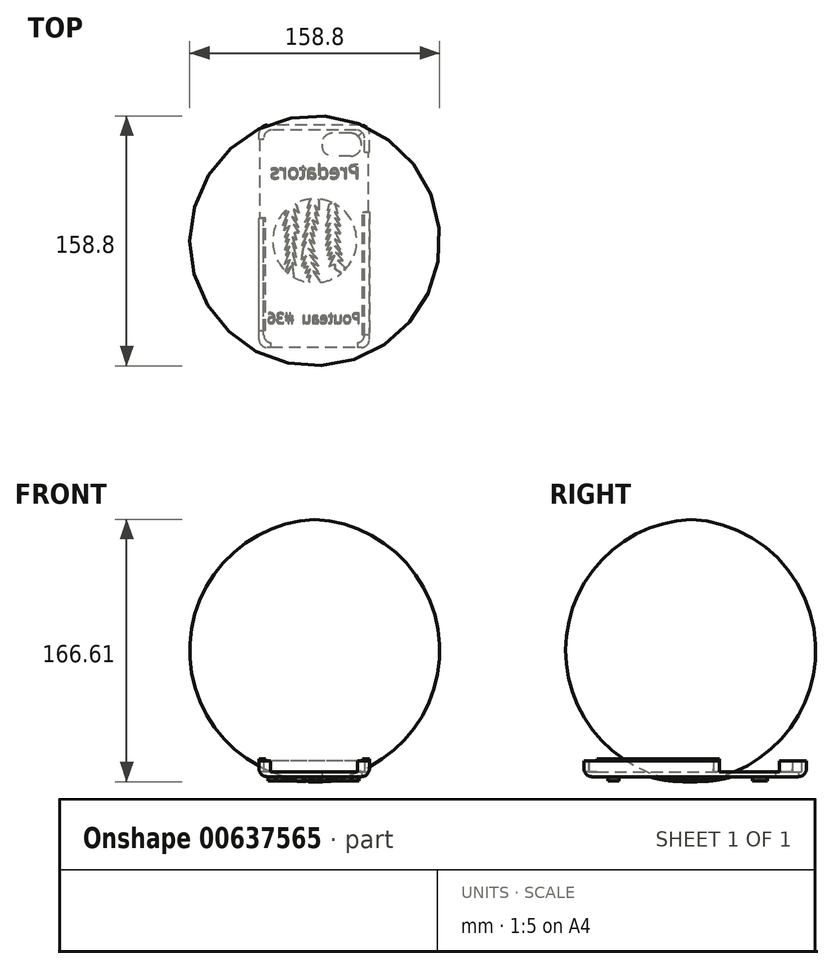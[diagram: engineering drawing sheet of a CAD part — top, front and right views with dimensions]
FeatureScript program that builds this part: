
annotation { "Feature Type Name" : "Feature", "Feature Type Description" : "" }
export const myFeature = defineFeature(function(context is Context, id is Id, definition is map)
    precondition{}
    {
        {
            var Q0;
            Q0=qCreatedBy(makeId("Top.planeOp"),FACE);
            var sketch = newSketch(context, id + "F0", { "sketchPlane" : qUnion([Q0])});
            skLineSegment(sketch, "E0.bottom", {"start": v(34.68, -26.2) * mm, "end": v(-35.42, -26.2) * mm});
            skLineSegment(sketch, "E0.top", {"start": v(34.68, 115.03) * mm, "end": v(-35.42, 115.03) * mm});
            skLineSegment(sketch, "E0.left", {"start": v(34.68, -26.2) * mm, "end": v(34.68, 115.03) * mm});
            skLineSegment(sketch, "E0.right", {"start": v(-35.42, -26.2) * mm, "end": v(-35.42, 115.03) * mm});
            skSolve(sketch);
        }
        {
            var Q0;
            Q0=makeQuery(id+"F0.imprint","IMPRINT",FACE,{"disambiguationData":[TD([[makeQuery(id+"F0.imprint","IMPRINT",EDGE,{"derivedFrom":sQuery(id+"F0.wireOp",EDGE,"E0.bottom")}),-1.0]])]});
            extrude(context, id + "F1", {"entities" : qUnion([Q0]), "depth" : 9.9 * mm, "offsetDistance" : 25.4 * mm});
        }
        {
            var Q0;
            Q0=makeQuery(id+"F1.opExtrude","CAP_FACE",FACE,{"disambiguationData":[OSD([sQuery(id+"F0.wireOp",EDGE,"E0.bottom"),sQuery(id+"F0.wireOp",EDGE,"E0.top"),sQuery(id+"F0.wireOp",EDGE,"E0.left"),sQuery(id+"F0.wireOp",EDGE,"E0.right")])],"isStart":false});
            shell(context, id + "F2", {"entities" : qUnion([Q0]), "thickness" : 3.05 * mm});
        }
        {
            var Q0;
            Q0=makeQuery(id+"F1.opExtrude","SWEPT_EDGE",EDGE,{"disambiguationData":[OSD([sQuery(id+"F0.wireOp",EDGE,"E0.top"),sQuery(id+"F0.wireOp",EDGE,"E0.right")])]});
            fillet(context, id + "F3", {"entities" : qUnion([Q0]), "radius" : 5.08 * mm, "tangentPropagation" : true, "allowEdgeOverflow" : false});
        }
        {
            var Q0;
            Q0=makeQuery(id+"F1.opExtrude","SWEPT_FACE",FACE,{"disambiguationData":[OSD([sQuery(id+"F0.wireOp",EDGE,"E0.right")])]});
            var sketch = newSketch(context, id + "F4", { "sketchPlane" : qUnion([Q0])});
            skLineSegment(sketch, "E1.bottom", {"start": v(-106.04, 9.9) * mm, "end": v(-56.04, 9.9) * mm});
            skLineSegment(sketch, "E1.top", {"start": v(-106.04, 3.05) * mm, "end": v(-56.04, 3.05) * mm});
            skLineSegment(sketch, "E1.left", {"start": v(-106.04, 9.9) * mm, "end": v(-106.04, 3.05) * mm});
            skLineSegment(sketch, "E1.right", {"start": v(-56.04, 9.9) * mm, "end": v(-56.04, 3.05) * mm});
            skSolve(sketch);
        }
        {
            var Q0;
            Q0=makeQuery(id+"F4.imprint","IMPRINT",FACE,{"disambiguationData":[TD([[makeQuery(id+"F4.imprint","IMPRINT",EDGE,{"derivedFrom":sQuery(id+"F4.wireOp",EDGE,"E1.bottom")}),1.0]])]});
            extrude(context, id + "F5", {"entities" : qUnion([Q0]), "operationType" : NewBodyOperationType.REMOVE, "oppositeDirection" : true, "depth" : 3.05 * mm, "offsetDistance" : 25.4 * mm});
        }
        {
            var Q0;
            Q0=makeQuery(id+"F1.opExtrude","SWEPT_FACE",FACE,{"disambiguationData":[OSD([sQuery(id+"F0.wireOp",EDGE,"E0.left")])]});
            var sketch = newSketch(context, id + "F6", { "sketchPlane" : qUnion([Q0])});
            skLineSegment(sketch, "E2.bottom", {"start": v(98, 9.9) * mm, "end": v(59.9, 9.9) * mm});
            skLineSegment(sketch, "E2.top", {"start": v(98, 3.05) * mm, "end": v(59.9, 3.05) * mm});
            skLineSegment(sketch, "E2.left", {"start": v(98, 9.9) * mm, "end": v(98, 3.05) * mm});
            skLineSegment(sketch, "E2.right", {"start": v(59.9, 9.9) * mm, "end": v(59.9, 3.05) * mm});
            skSolve(sketch);
        }
        {
            var Q0;
            Q0=makeQuery(id+"F6.imprint","IMPRINT",FACE,{"disambiguationData":[TD([[makeQuery(id+"F6.imprint","IMPRINT",EDGE,{"derivedFrom":sQuery(id+"F6.wireOp",EDGE,"E2.bottom")}),-1.0]])]});
            extrude(context, id + "F7", {"entities" : qUnion([Q0]), "operationType" : NewBodyOperationType.REMOVE, "oppositeDirection" : true, "depth" : 3.05 * mm, "offsetDistance" : 25.4 * mm});
        }
        {
            var Q0;
            Q0=makeQuery(id+"F1.opExtrude","SWEPT_EDGE",EDGE,{"disambiguationData":[OSD([sQuery(id+"F0.wireOp",EDGE,"E0.top"),sQuery(id+"F0.wireOp",EDGE,"E0.left")])]});
            var Q1;
            Q1=makeQuery(id+"F2.opShell","OFFSET_EDGE",EDGE,{"disambiguationData":[OSD([sQuery(id+"F0.wireOp",EDGE,"E0.top"),sQuery(id+"F0.wireOp",EDGE,"E0.left")])]});
            var Q2;
            Q2=makeQuery(id+"F2.opShell","OFFSET_EDGE",EDGE,{"disambiguationData":[OSD([sQuery(id+"F0.wireOp",EDGE,"E0.top"),sQuery(id+"F0.wireOp",EDGE,"E0.right")])]});
            var Q3;
            Q3=makeQuery(id+"F1.opExtrude","SWEPT_EDGE",EDGE,{"disambiguationData":[OSD([sQuery(id+"F0.wireOp",EDGE,"E0.bottom"),sQuery(id+"F0.wireOp",EDGE,"E0.left")])]});
            var Q4;
            Q4=makeQuery(id+"F1.opExtrude","SWEPT_EDGE",EDGE,{"disambiguationData":[OSD([sQuery(id+"F0.wireOp",EDGE,"E0.bottom"),sQuery(id+"F0.wireOp",EDGE,"E0.right")])]});
            var Q5;
            Q5=makeQuery(id+"F2.opShell","OFFSET_EDGE",EDGE,{"disambiguationData":[OSD([sQuery(id+"F0.wireOp",EDGE,"E0.bottom"),sQuery(id+"F0.wireOp",EDGE,"E0.right")])]});
            var Q6;
            Q6=makeQuery(id+"F2.opShell","OFFSET_EDGE",EDGE,{"disambiguationData":[OSD([sQuery(id+"F0.wireOp",EDGE,"E0.bottom"),sQuery(id+"F0.wireOp",EDGE,"E0.left")])]});
            fillet(context, id + "F8", {"entities" : qUnion([Q0, Q1, Q2, Q3, Q4, Q5, Q6]), "radius" : 5.08 * mm, "tangentPropagation" : true, "allowEdgeOverflow" : false});
        }
        {
            var Q0;
            Q0=makeQuery(id+"F1.opExtrude","SWEPT_FACE",FACE,{"disambiguationData":[OSD([sQuery(id+"F0.wireOp",EDGE,"E0.bottom")])]});
            var sketch = newSketch(context, id + "F9", { "sketchPlane" : qUnion([Q0])});
            skLineSegment(sketch, "E3.bottom", {"start": v(-27.96, 9.9) * mm, "end": v(27.04, 9.9) * mm});
            skLineSegment(sketch, "E3.top", {"start": v(-27.96, 3.05) * mm, "end": v(27.04, 3.05) * mm});
            skLineSegment(sketch, "E3.left", {"start": v(-27.96, 9.9) * mm, "end": v(-27.96, 3.05) * mm});
            skLineSegment(sketch, "E3.right", {"start": v(27.04, 9.9) * mm, "end": v(27.04, 3.05) * mm});
            skSolve(sketch);
        }
        {
            var Q0;
            Q0=makeQuery(id+"F9.imprint","IMPRINT",FACE,{"disambiguationData":[TD([[makeQuery(id+"F9.imprint","IMPRINT",EDGE,{"derivedFrom":sQuery(id+"F9.wireOp",EDGE,"E3.bottom")}),1.0]])]});
            extrude(context, id + "F10", {"entities" : qUnion([Q0]), "operationType" : NewBodyOperationType.REMOVE, "oppositeDirection" : true, "depth" : 3.56 * mm, "offsetDistance" : 25.4 * mm});
        }
        {
            var Q0;
            Q0=makeQuery(id+"F1.opExtrude","CAP_EDGE",EDGE,{"disambiguationData":[OSD([sQuery(id+"F0.wireOp",EDGE,"E0.top")])],"isStart":true});
            var Q1;
            Q1=makeQuery(id+"F1.opExtrude","CAP_FACE",FACE,{"disambiguationData":[OSD([sQuery(id+"F0.wireOp",EDGE,"E0.bottom"),sQuery(id+"F0.wireOp",EDGE,"E0.top"),sQuery(id+"F0.wireOp",EDGE,"E0.left"),sQuery(id+"F0.wireOp",EDGE,"E0.right")])],"isStart":true});
            fillet(context, id + "F11", {"entities" : qUnion([Q0, Q1]), "radius" : 5.08 * mm, "tangentPropagation" : true, "allowEdgeOverflow" : false});
        }
        {
            var Q0;
            Q0=makeQuery(id+"F1.opExtrude","CAP_FACE",FACE,{"disambiguationData":[OSD([sQuery(id+"F0.wireOp",EDGE,"E0.bottom"),sQuery(id+"F0.wireOp",EDGE,"E0.top"),sQuery(id+"F0.wireOp",EDGE,"E0.left"),sQuery(id+"F0.wireOp",EDGE,"E0.right")])],"isStart":true});
            var sketch = newSketch(context, id + "F12", { "sketchPlane" : qUnion([Q0])});
            skLineSegment(sketch, "E4.bottom", {"start": v(29.6, -109.95) * mm, "end": v(4.52, -109.95) * mm});
            skLineSegment(sketch, "E4.top", {"start": v(29.6, -95.42) * mm, "end": v(4.52, -95.42) * mm});
            skLineSegment(sketch, "E4.left", {"start": v(29.6, -109.95) * mm, "end": v(29.6, -95.42) * mm});
            skLineSegment(sketch, "E4.right", {"start": v(4.52, -109.95) * mm, "end": v(4.52, -95.42) * mm});
            skSolve(sketch);
        }
        {
            var Q0;
            Q0=makeQuery(id+"F12.imprint","IMPRINT",FACE,{"disambiguationData":[TD([[makeQuery(id+"F12.imprint","IMPRINT",EDGE,{"derivedFrom":sQuery(id+"F12.wireOp",EDGE,"E4.bottom")}),1.0]])]});
            extrude(context, id + "F13", {"entities" : qUnion([Q0]), "operationType" : NewBodyOperationType.REMOVE, "oppositeDirection" : true, "depth" : 3.05 * mm, "offsetDistance" : 25.4 * mm});
        }
        {
            var Q0;
            {var subQ0=sQuery(id+"F0.wireOp",EDGE,"E0.bottom");var subQ2=sQuery(id+"F0.wireOp",EDGE,"E0.left");Q0=makeQuery(id+"F7.boolean.opBoolean","SPLIT",FACE,{"disambiguationData":[TD([makeQuery(id+"F2.opShell","OFFSET_FACE",FACE,{"disambiguationData":[OSD([subQ0])]})])],"derivedFrom":makeQuery(id+"F2.opShell","OFFSET_FACE",FACE,{"disambiguationData":[OSD([subQ2])]})});}
            var sketch = newSketch(context, id + "F14", { "sketchPlane" : qUnion([Q0])});
            skLineSegment(sketch, "E5.bottom", {"start": v(-59.9, 9.9) * mm, "end": v(18.07, 9.9) * mm});
            skLineSegment(sketch, "E5.top", {"start": v(-59.9, 11.18) * mm, "end": v(18.07, 11.18) * mm});
            skLineSegment(sketch, "E5.left", {"start": v(-59.9, 9.9) * mm, "end": v(-59.9, 11.18) * mm});
            skLineSegment(sketch, "E5.right", {"start": v(18.07, 9.9) * mm, "end": v(18.07, 11.18) * mm});
            skSolve(sketch);
        }
        {
            var Q0;
            Q0 = qSketchRegion(id + "F14", true);
            extrude(context, id + "F15", {"entities" : qUnion([Q0]), "depth" : 1.27 * mm, "offsetDistance" : 25.4 * mm});
        }
        {
            var Q0;
            Q0=makeQuery(id+"F15.opExtrude","CAP_FACE",FACE,{"disambiguationData":[OSD([sQuery(id+"F14.wireOp",EDGE,"E5.bottom"),sQuery(id+"F14.wireOp",EDGE,"E5.top"),sQuery(id+"F14.wireOp",EDGE,"E5.left"),sQuery(id+"F14.wireOp",EDGE,"E5.right")])],"isStart":true});
            extrude(context, id + "F16", {"entities" : qUnion([Q0]), "depth" : 3.05 * mm, "offsetDistance" : 25.4 * mm});
        }
        {
            var Q0;
            {var subQ0=sQuery(id+"F0.wireOp",EDGE,"E0.bottom");var subQ1=sQuery(id+"F0.wireOp",EDGE,"E0.right");Q0=makeQuery(id+"F5.boolean.opBoolean","SPLIT",FACE,{"disambiguationData":[TD([makeQuery(id+"F2.opShell","OFFSET_FACE",FACE,{"disambiguationData":[OSD([subQ0])]})])],"derivedFrom":makeQuery(id+"F2.opShell","OFFSET_FACE",FACE,{"disambiguationData":[OSD([subQ1])]})});}
            var sketch = newSketch(context, id + "F17", { "sketchPlane" : qUnion([Q0])});
            skLineSegment(sketch, "E6.bottom", {"start": v(56.04, 9.9) * mm, "end": v(-15.42, 9.9) * mm});
            skLineSegment(sketch, "E6.top", {"start": v(56.04, 11.18) * mm, "end": v(-15.42, 11.18) * mm});
            skLineSegment(sketch, "E6.left", {"start": v(56.04, 9.9) * mm, "end": v(56.04, 11.18) * mm});
            skLineSegment(sketch, "E6.right", {"start": v(-15.42, 9.9) * mm, "end": v(-15.42, 11.18) * mm});
            skSolve(sketch);
        }
        {
            var Q0;
            Q0=makeQuery(id+"F17.imprint","IMPRINT",FACE,{"disambiguationData":[TD([[makeQuery(id+"F17.imprint","IMPRINT",EDGE,{"derivedFrom":sQuery(id+"F17.wireOp",EDGE,"E6.bottom")}),1.0]])]});
            extrude(context, id + "F18", {"entities" : qUnion([Q0]), "depth" : 1.27 * mm, "offsetDistance" : 25.4 * mm});
        }
        {
            var Q0;
            Q0=makeQuery(id+"F18.opExtrude","CAP_FACE",FACE,{"disambiguationData":[OSD([sQuery(id+"F17.wireOp",EDGE,"E6.bottom"),sQuery(id+"F17.wireOp",EDGE,"E6.top"),sQuery(id+"F17.wireOp",EDGE,"E6.left"),sQuery(id+"F17.wireOp",EDGE,"E6.right")])],"isStart":true});
            extrude(context, id + "F19", {"entities" : qUnion([Q0]), "depth" : 3.05 * mm, "offsetDistance" : 25.4 * mm});
        }
        {
            var Q0;
            Q0=makeQuery(id+"F1.opExtrude","CAP_FACE",FACE,{"disambiguationData":[OSD([sQuery(id+"F0.wireOp",EDGE,"E0.bottom"),sQuery(id+"F0.wireOp",EDGE,"E0.top"),sQuery(id+"F0.wireOp",EDGE,"E0.left"),sQuery(id+"F0.wireOp",EDGE,"E0.right")])],"isStart":true});
            var sketch = newSketch(context, id + "F20", { "sketchPlane" : qUnion([Q0])});
            skText(sketch, "E7", { "text": "Predators\n", "fontName": "OpenSans-Regular.ttf"});
            skPoint(sketch, "E8.center.orphan", {"position": v(0, -41.54) * mm});
            const initialGuessF20  = {"E7": [0.02862, -0.08103, -1, 0, 0.00896]};
            skSetInitialGuess(sketch, initialGuessF20);
            skSolve(sketch);
        }
        {
            var Q0;
            Q0=qCreatedBy(makeId("Right.planeOp"),FACE);
            var sketch = newSketch(context, id + "F21", { "sketchPlane" : qUnion([Q0])});
            skLineSegment(sketch, "E9", {"start": v(41.6, 0) * mm, "end": v(41.6, -3.06) * mm});
            skArc(sketch, "E10", {"start": v(14.92, 0) * mm, "mid": v(28.13, -2.61) * mm, "end": v(41.6, -3.06) * mm});
            skLineSegment(sketch, "E11", {"start": v(41.6, 0) * mm, "end": v(14.92, 0) * mm});
            skSolve(sketch);
        }
        {
            var Q0;
            Q0=makeQuery(id+"F21.imprint","IMPRINT",FACE,{"disambiguationData":[TD([[makeQuery(id+"F21.imprint","IMPRINT",EDGE,{"derivedFrom":sQuery(id+"F21.wireOp",EDGE,"E9")}),-1.0]])]});
            var Q1;
            Q1=sQuery(id+"F21.wireOp",EDGE,"E9");
            revolve(context, id + "F22", {"operationType" : NewBodyOperationType.ADD, "entities" : qUnion([Q0]), "axis" : qUnion([Q1]), "revolveType" : RevolveType.FULL});
        }
        {
            var Q0;
            Q0=makeQuery(id+"F20.imprint","IMPRINT",FACE,{"disambiguationData":[TD([[makeQuery(id+"F20.imprint","IMPRINT",EDGE,{"derivedFrom":sQuery(id+"F20.wireOp",EDGE,"E7.sketch_text.stroke-0")}),1.0]])]});
            var sketch = newSketch(context, id + "F23", { "sketchPlane" : qUnion([Q0])});
            skLineSegment(sketch, "E12", {"start": v(13.28, -64.28) * mm, "end": v(14.6, -58.78) * mm});
            skLineSegment(sketch, "E13", {"start": v(14.6, -58.78) * mm, "end": v(12.69, -59.98) * mm});
            skLineSegment(sketch, "E14", {"start": v(12.69, -59.98) * mm, "end": v(15.8, -54.84) * mm});
            skLineSegment(sketch, "E15", {"start": v(15.8, -54.84) * mm, "end": v(12.8, -56.04) * mm});
            skLineSegment(sketch, "E16", {"start": v(12.8, -56.04) * mm, "end": v(16.27, -50.9) * mm});
            skLineSegment(sketch, "E17", {"start": v(16.27, -50.9) * mm, "end": v(12.69, -52.33) * mm});
            skLineSegment(sketch, "E18", {"start": v(12.69, -52.33) * mm, "end": v(16.27, -46.12) * mm});
            skLineSegment(sketch, "E19", {"start": v(16.27, -46.12) * mm, "end": v(13.04, -47.2) * mm});
            skLineSegment(sketch, "E20", {"start": v(13.04, -47.2) * mm, "end": v(16.27, -40.63) * mm});
            skLineSegment(sketch, "E21", {"start": v(16.27, -40.63) * mm, "end": v(12.69, -42.78) * mm});
            skLineSegment(sketch, "E22", {"start": v(12.69, -42.78) * mm, "end": v(16.27, -36.09) * mm});
            skLineSegment(sketch, "E23", {"start": v(16.27, -36.09) * mm, "end": v(12.8, -38.24) * mm});
            skLineSegment(sketch, "E24", {"start": v(12.8, -38.24) * mm, "end": v(17.34, -32.74) * mm});
            skLineSegment(sketch, "E25", {"start": v(17.34, -32.74) * mm, "end": v(13.28, -34.3) * mm});
            skLineSegment(sketch, "E26", {"start": v(13.28, -34.3) * mm, "end": v(18.06, -29.04) * mm});
            skLineSegment(sketch, "E27", {"start": v(18.06, -29.04) * mm, "end": v(14.6, -29.04) * mm});
            skLineSegment(sketch, "E28", {"start": v(14.6, -29.04) * mm, "end": v(18.9, -24.98) * mm});
            skLineSegment(sketch, "E29", {"start": v(9.22, -64.64) * mm, "end": v(8.15, -60.7) * mm});
            skLineSegment(sketch, "E30", {"start": v(8.15, -60.7) * mm, "end": v(9.46, -61.77) * mm});
            skLineSegment(sketch, "E31", {"start": v(9.46, -61.77) * mm, "end": v(7.87, -55.95) * mm});
            skLineSegment(sketch, "E32", {"start": v(7.87, -55.95) * mm, "end": v(9.82, -57.95) * mm});
            skLineSegment(sketch, "E33", {"start": v(9.82, -57.95) * mm, "end": v(6.95, -50.9) * mm});
            skLineSegment(sketch, "E34", {"start": v(6.95, -50.9) * mm, "end": v(9.94, -52.81) * mm});
            skLineSegment(sketch, "E35", {"start": v(9.94, -52.81) * mm, "end": v(6.95, -46.84) * mm});
            skLineSegment(sketch, "E36", {"start": v(6.95, -46.84) * mm, "end": v(9.94, -48.87) * mm});
            skLineSegment(sketch, "E37", {"start": v(9.94, -48.87) * mm, "end": v(6.95, -42.3) * mm});
            skLineSegment(sketch, "E38", {"start": v(6.95, -42.3) * mm, "end": v(10.18, -45.58) * mm});
            skPoint(sketch, "E38.endSnap0", {"position": v(8.44, -45.58) * mm});
            skLineSegment(sketch, "E39", {"start": v(10.18, -45.58) * mm, "end": v(6.95, -38.49) * mm});
            skLineSegment(sketch, "E40", {"start": v(6.95, -38.49) * mm, "end": v(10.06, -41.1) * mm});
            skLineSegment(sketch, "E41", {"start": v(10.06, -41.1) * mm, "end": v(7.64, -35.79) * mm});
            skLineSegment(sketch, "E42", {"start": v(7.64, -35.79) * mm, "end": v(10.3, -37.28) * mm});
            skLineSegment(sketch, "E43", {"start": v(10.3, -37.28) * mm, "end": v(8, -32.24) * mm});
            skLineSegment(sketch, "E44", {"start": v(8, -32.24) * mm, "end": v(11.01, -34.18) * mm});
            skLineSegment(sketch, "E45", {"start": v(11.01, -34.18) * mm, "end": v(8.94, -29.62) * mm});
            skLineSegment(sketch, "E46", {"start": v(8.94, -29.62) * mm, "end": v(12.45, -32.38) * mm});
            skLineSegment(sketch, "E47", {"start": v(12.45, -32.38) * mm, "end": v(9.2, -25.26) * mm});
            skLineSegment(sketch, "E48", {"start": v(9.2, -25.26) * mm, "end": v(12.92, -26.77) * mm});
            skLineSegment(sketch, "E49", {"start": v(12.92, -26.77) * mm, "end": v(12.92, -23.66) * mm});
            skLineSegment(sketch, "E50", {"start": v(13.28, -64.28) * mm, "end": v(11.5, -66.31) * mm});
            skLineSegment(sketch, "E51", {"start": v(11.5, -66.31) * mm, "end": v(9.22, -64.64) * mm});
            skLineSegment(sketch, "E52", {"start": v(18.9, -24.98) * mm, "end": v(18.9, -19.74) * mm});
            skLineSegment(sketch, "E53", {"start": v(18.9, -19.74) * mm, "end": v(12.92, -23.66) * mm});
            skLineSegment(sketch, "E54", {"start": v(2.8, -67.4) * mm, "end": v(2.8, -61.16) * mm});
            skLineSegment(sketch, "E55", {"start": v(2.8, -61.16) * mm, "end": v(0, -64.28) * mm});
            skLineSegment(sketch, "E56", {"start": v(0, -64.28) * mm, "end": v(2.5, -57.27) * mm});
            skLineSegment(sketch, "E57", {"start": v(2.5, -57.27) * mm, "end": v(0, -59.52) * mm});
            skLineSegment(sketch, "E58", {"start": v(0, -59.52) * mm, "end": v(2.04, -52.6) * mm});
            skLineSegment(sketch, "E59", {"start": v(2.04, -52.6) * mm, "end": v(-1.49, -54.89) * mm});
            skLineSegment(sketch, "E60", {"start": v(-1.49, -54.89) * mm, "end": v(1.22, -48.34) * mm});
            skLineSegment(sketch, "E61", {"start": v(1.22, -48.34) * mm, "end": v(-2, -50.8) * mm});
            skLineSegment(sketch, "E62", {"start": v(-2, -50.8) * mm, "end": v(0, -44.26) * mm});
            skLineSegment(sketch, "E63", {"start": v(0, -44.26) * mm, "end": v(-2.67, -46.74) * mm});
            skLineSegment(sketch, "E64", {"start": v(-2.67, -46.74) * mm, "end": v(0, -39.77) * mm});
            skLineSegment(sketch, "E65", {"start": v(0, -39.77) * mm, "end": v(-3.52, -42.28) * mm});
            skLineSegment(sketch, "E66", {"start": v(-3.52, -42.28) * mm, "end": v(0, -34.89) * mm});
            skLineSegment(sketch, "E67", {"start": v(0, -34.89) * mm, "end": v(-4.35, -36.85) * mm});
            skLineSegment(sketch, "E68", {"start": v(-4.35, -36.85) * mm, "end": v(1.75, -30.38) * mm});
            skLineSegment(sketch, "E69", {"start": v(1.75, -30.38) * mm, "end": v(-3.2, -32.52) * mm});
            skLineSegment(sketch, "E70", {"start": v(-3.2, -32.52) * mm, "end": v(2.57, -25.66) * mm});
            skLineSegment(sketch, "E71", {"start": v(2.57, -25.66) * mm, "end": v(-2.25, -27.8) * mm});
            skLineSegment(sketch, "E72", {"start": v(-2.25, -27.8) * mm, "end": v(2.9, -20.58) * mm});
            skLineSegment(sketch, "E73", {"start": v(2.9, -20.58) * mm, "end": v(-1.23, -22.5) * mm});
            skLineSegment(sketch, "E74", {"start": v(3.9, -15.08) * mm, "end": v(0, -11.67) * mm});
            skLineSegment(sketch, "E75", {"start": v(0, -11.67) * mm, "end": v(-3.8, -16.04) * mm});
            skLineSegment(sketch, "E76", {"start": v(2.8, -67.4) * mm, "end": v(0, -70.04) * mm});
            skLineSegment(sketch, "E77", {"start": v(0, -70.04) * mm, "end": v(-2.93, -67.4) * mm});
            skLineSegment(sketch, "E78", {"start": v(-2.93, -67.4) * mm, "end": v(-4.8, -62.23) * mm});
            skLineSegment(sketch, "E79", {"start": v(-4.8, -62.23) * mm, "end": v(-2.51, -64.28) * mm});
            skLineSegment(sketch, "E80", {"start": v(-2.51, -64.28) * mm, "end": v(-5.41, -57.38) * mm});
            skLineSegment(sketch, "E81", {"start": v(-5.41, -57.38) * mm, "end": v(-2.93, -59.6) * mm});
            skLineSegment(sketch, "E82", {"start": v(-2.93, -59.6) * mm, "end": v(-6.36, -53.32) * mm});
            skLineSegment(sketch, "E83", {"start": v(-6.36, -53.32) * mm, "end": v(-2.93, -56.4) * mm});
            skLineSegment(sketch, "E84", {"start": v(-2.93, -56.4) * mm, "end": v(-6.07, -49.99) * mm});
            skLineSegment(sketch, "E85", {"start": v(-6.07, -49.99) * mm, "end": v(-3.64, -52.43) * mm});
            skLineSegment(sketch, "E86", {"start": v(-3.64, -52.43) * mm, "end": v(-7.69, -44) * mm});
            skLineSegment(sketch, "E87", {"start": v(-7.69, -44) * mm, "end": v(-4.71, -46.23) * mm});
            skLineSegment(sketch, "E88", {"start": v(-4.71, -46.23) * mm, "end": v(-8.07, -38.75) * mm});
            skLineSegment(sketch, "E89", {"start": v(-8.07, -38.75) * mm, "end": v(-5.66, -40.92) * mm});
            skLineSegment(sketch, "E90", {"start": v(-5.66, -40.92) * mm, "end": v(-8.2, -34.46) * mm});
            skLineSegment(sketch, "E91", {"start": v(-8.2, -34.46) * mm, "end": v(-7.4, -36.48) * mm});
            skLineSegment(sketch, "E92", {"start": v(-7.4, -36.48) * mm, "end": v(-8.4, -29.6) * mm});
            skLineSegment(sketch, "E93", {"start": v(-8.4, -29.6) * mm, "end": v(-5.69, -32.02) * mm});
            skLineSegment(sketch, "E94", {"start": v(-5.69, -32.02) * mm, "end": v(-8.3, -25.37) * mm});
            skLineSegment(sketch, "E95", {"start": v(-8.3, -25.37) * mm, "end": v(-5.48, -27.9) * mm});
            skLineSegment(sketch, "E96", {"start": v(-5.48, -27.9) * mm, "end": v(-6.95, -24.17) * mm});
            skLineSegment(sketch, "E97", {"start": v(-6.95, -24.17) * mm, "end": v(-4.24, -25.53) * mm});
            skLineSegment(sketch, "E98", {"start": v(-4.24, -25.53) * mm, "end": v(-6.15, -20.68) * mm});
            skLineSegment(sketch, "E99", {"start": v(-6.15, -20.68) * mm, "end": v(-2.93, -23.57) * mm});
            skLineSegment(sketch, "E100", {"start": v(-2.93, -23.57) * mm, "end": v(-5.04, -18.2) * mm});
            skLineSegment(sketch, "E101", {"start": v(-11.58, -64.28) * mm, "end": v(-14.39, -67.4) * mm});
            skLineSegment(sketch, "E102", {"start": v(-14.39, -67.4) * mm, "end": v(-17.66, -62.33) * mm});
            skLineSegment(sketch, "E103", {"start": v(-17.66, -62.33) * mm, "end": v(-19.44, -57.95) * mm});
            skLineSegment(sketch, "E104", {"start": v(-19.44, -57.95) * mm, "end": v(-16.64, -60.34) * mm});
            skLineSegment(sketch, "E105", {"start": v(-16.64, -60.34) * mm, "end": v(-20.37, -51.17) * mm});
            skLineSegment(sketch, "E106", {"start": v(-20.37, -51.17) * mm, "end": v(-17.6, -55.1) * mm});
            skLineSegment(sketch, "E107", {"start": v(-17.6, -55.1) * mm, "end": v(-19.47, -48.16) * mm});
            skLineSegment(sketch, "E108", {"start": v(-19.47, -48.16) * mm, "end": v(-16.13, -51.16) * mm});
            skLineSegment(sketch, "E109", {"start": v(-16.13, -51.16) * mm, "end": v(-19.13, -43.79) * mm});
            skLineSegment(sketch, "E110", {"start": v(-19.13, -43.79) * mm, "end": v(-16.5, -45.9) * mm});
            skLineSegment(sketch, "E111", {"start": v(-16.5, -45.9) * mm, "end": v(-18.54, -40.9) * mm});
            skLineSegment(sketch, "E112", {"start": v(-18.54, -40.9) * mm, "end": v(-16.2, -42.76) * mm});
            skLineSegment(sketch, "E113", {"start": v(-16.2, -42.76) * mm, "end": v(-19.01, -35.84) * mm});
            skLineSegment(sketch, "E114", {"start": v(-19.01, -35.84) * mm, "end": v(-16.09, -38.08) * mm});
            skLineSegment(sketch, "E115", {"start": v(-16.09, -38.08) * mm, "end": v(-18.4, -32.38) * mm});
            skLineSegment(sketch, "E116", {"start": v(-18.4, -32.38) * mm, "end": v(-15.9, -34.63) * mm});
            skLineSegment(sketch, "E117", {"start": v(-15.9, -34.63) * mm, "end": v(-19.12, -26.7) * mm});
            skLineSegment(sketch, "E118", {"start": v(-19.12, -26.7) * mm, "end": v(-15.7, -29.78) * mm});
            skLineSegment(sketch, "E119", {"start": v(-15.7, -29.78) * mm, "end": v(-18.68, -22.18) * mm});
            skLineSegment(sketch, "E120", {"start": v(-18.68, -22.18) * mm, "end": v(-15.19, -25.32) * mm});
            skLineSegment(sketch, "E121", {"start": v(-15.19, -25.32) * mm, "end": v(-18.1, -18.17) * mm});
            skLineSegment(sketch, "E122", {"start": v(-18.1, -18.17) * mm, "end": v(-15.13, -14.88) * mm});
            skLineSegment(sketch, "E123", {"start": v(-15.13, -14.88) * mm, "end": v(-13.22, -19.59) * mm});
            skLineSegment(sketch, "E124", {"start": v(-11.58, -64.28) * mm, "end": v(-10.12, -59.31) * mm});
            skLineSegment(sketch, "E125", {"start": v(-10.12, -59.31) * mm, "end": v(-13.37, -61.8) * mm});
            skPoint(sketch, "E125.endSnap0", {"position": v(-10.85, -61.8) * mm});
            skLineSegment(sketch, "E126", {"start": v(-13.37, -61.8) * mm, "end": v(-11.29, -54.72) * mm});
            skLineSegment(sketch, "E127", {"start": v(-11.29, -54.72) * mm, "end": v(-14.53, -56.94) * mm});
            skLineSegment(sketch, "E128", {"start": v(-14.53, -56.94) * mm, "end": v(-10.12, -50.14) * mm});
            skLineSegment(sketch, "E129", {"start": v(-10.12, -50.14) * mm, "end": v(-13.46, -52.02) * mm});
            skLineSegment(sketch, "E130", {"start": v(-13.46, -52.02) * mm, "end": v(-10.12, -46.83) * mm});
            skLineSegment(sketch, "E131", {"start": v(-10.12, -46.83) * mm, "end": v(-13, -46.83) * mm});
            skLineSegment(sketch, "E132", {"start": v(-13, -46.83) * mm, "end": v(-11.6, -42.1) * mm});
            skLineSegment(sketch, "E133", {"start": v(-11.6, -42.1) * mm, "end": v(-14.05, -44.05) * mm});
            skLineSegment(sketch, "E134", {"start": v(-14.05, -44.05) * mm, "end": v(-11.93, -36.82) * mm});
            skLineSegment(sketch, "E135", {"start": v(-11.93, -36.82) * mm, "end": v(-14.29, -40.44) * mm});
            skPoint(sketch, "E135.endSnap0", {"position": v(-12.99, -40.44) * mm});
            skLineSegment(sketch, "E136", {"start": v(-14.29, -40.44) * mm, "end": v(-11.57, -31.18) * mm});
            skLineSegment(sketch, "E137", {"start": v(-11.57, -31.18) * mm, "end": v(-14.19, -34.1) * mm});
            skLineSegment(sketch, "E138", {"start": v(-14.19, -34.1) * mm, "end": v(-11.8, -25.98) * mm});
            skLineSegment(sketch, "E139", {"start": v(-11.8, -25.98) * mm, "end": v(-14.28, -27.86) * mm});
            skLineSegment(sketch, "E140", {"start": v(-14.28, -27.86) * mm, "end": v(-13.22, -19.59) * mm});
            skLineSegment(sketch, "E141", {"start": v(-1.23, -22.5) * mm, "end": v(3.9, -15.08) * mm});
            skLineSegment(sketch, "E142", {"start": v(-5.04, -18.2) * mm, "end": v(-2.65, -19.61) * mm});
            skLineSegment(sketch, "E143", {"start": v(-2.65, -19.61) * mm, "end": v(-3.8, -16.04) * mm});
            skSolve(sketch);
        }
        {
            var Q0;
            Q0 = qSketchRegion(id + "F20", true);
            extrude(context, id + "F24", {"entities" : qUnion([Q0]), "operationType" : NewBodyOperationType.ADD, "depth" : 2.54 * mm, "offsetDistance" : 25.4 * mm});
        }
        {
            var Q0;
            Q0 = qSketchRegion(id + "F23", true);
            extrude(context, id + "F25", {"entities" : qUnion([Q0]), "operationType" : NewBodyOperationType.REMOVE, "depth" : 6.35 * mm, "offsetDistance" : 25.4 * mm});
        }
        {
            var Q0;
            {var subQ0=sQuery(id+"F0.wireOp",EDGE,"E0.right");var subQ1=sQuery(id+"F0.wireOp",EDGE,"E0.bottom");var subQ2=sQuery(id+"F0.wireOp",EDGE,"E0.left");var subQ3=sQuery(id+"F0.wireOp",EDGE,"E0.top");var subQ4=makeQuery(id+"F1.opExtrude","CAP_FACE",FACE,{"disambiguationData":[OSD([subQ1,subQ3,subQ2,subQ0])],"isStart":true});var subQ5=subQ4;Q0=makeQuery(id+"F25.boolean.opBoolean","MERGE",FACE,{"derivedFrom":[makeQuery(id+"F24.boolean.opBoolean","SPLIT",FACE,{"disambiguationData":[TD([makeQuery(id+"F11.opFillet","BLEND_FACE",FACE,{"disambiguationData":[OSD([subQ1])]})])],"derivedFrom":subQ5}),makeQuery(id+"F25.opExtrude","CAP_FACE",FACE,{"disambiguationData":[OSD([sQuery(id+"F23.wireOp",EDGE,"E12"),sQuery(id+"F23.wireOp",EDGE,"E13"),sQuery(id+"F23.wireOp",EDGE,"E14"),sQuery(id+"F23.wireOp",EDGE,"E15"),sQuery(id+"F23.wireOp",EDGE,"E16"),sQuery(id+"F23.wireOp",EDGE,"E17"),sQuery(id+"F23.wireOp",EDGE,"E18"),sQuery(id+"F23.wireOp",EDGE,"E19"),sQuery(id+"F23.wireOp",EDGE,"E20"),sQuery(id+"F23.wireOp",EDGE,"E21"),sQuery(id+"F23.wireOp",EDGE,"E22"),sQuery(id+"F23.wireOp",EDGE,"E23"),sQuery(id+"F23.wireOp",EDGE,"E24"),sQuery(id+"F23.wireOp",EDGE,"E25"),sQuery(id+"F23.wireOp",EDGE,"E26"),sQuery(id+"F23.wireOp",EDGE,"E27"),sQuery(id+"F23.wireOp",EDGE,"E28"),sQuery(id+"F23.wireOp",EDGE,"E29"),sQuery(id+"F23.wireOp",EDGE,"E30"),sQuery(id+"F23.wireOp",EDGE,"E31"),sQuery(id+"F23.wireOp",EDGE,"E32"),sQuery(id+"F23.wireOp",EDGE,"E33"),sQuery(id+"F23.wireOp",EDGE,"E34"),sQuery(id+"F23.wireOp",EDGE,"E35"),sQuery(id+"F23.wireOp",EDGE,"E36"),sQuery(id+"F23.wireOp",EDGE,"E37"),sQuery(id+"F23.wireOp",EDGE,"E38"),sQuery(id+"F23.wireOp",EDGE,"E39"),sQuery(id+"F23.wireOp",EDGE,"E40"),sQuery(id+"F23.wireOp",EDGE,"E41"),sQuery(id+"F23.wireOp",EDGE,"E42"),sQuery(id+"F23.wireOp",EDGE,"E43"),sQuery(id+"F23.wireOp",EDGE,"E44"),sQuery(id+"F23.wireOp",EDGE,"E45"),sQuery(id+"F23.wireOp",EDGE,"E46"),sQuery(id+"F23.wireOp",EDGE,"E47"),sQuery(id+"F23.wireOp",EDGE,"E48"),sQuery(id+"F23.wireOp",EDGE,"E49"),sQuery(id+"F23.wireOp",EDGE,"E50"),sQuery(id+"F23.wireOp",EDGE,"E51"),sQuery(id+"F23.wireOp",EDGE,"E52"),sQuery(id+"F23.wireOp",EDGE,"E53")])],"isStart":true}),makeQuery(id+"F25.opExtrude","CAP_FACE",FACE,{"disambiguationData":[OSD([sQuery(id+"F23.wireOp",EDGE,"E54"),sQuery(id+"F23.wireOp",EDGE,"E55"),sQuery(id+"F23.wireOp",EDGE,"E56"),sQuery(id+"F23.wireOp",EDGE,"E57"),sQuery(id+"F23.wireOp",EDGE,"E58"),sQuery(id+"F23.wireOp",EDGE,"E59"),sQuery(id+"F23.wireOp",EDGE,"E60"),sQuery(id+"F23.wireOp",EDGE,"E61"),sQuery(id+"F23.wireOp",EDGE,"E62"),sQuery(id+"F23.wireOp",EDGE,"E63"),sQuery(id+"F23.wireOp",EDGE,"E64"),sQuery(id+"F23.wireOp",EDGE,"E65"),sQuery(id+"F23.wireOp",EDGE,"E66"),sQuery(id+"F23.wireOp",EDGE,"E67"),sQuery(id+"F23.wireOp",EDGE,"E68"),sQuery(id+"F23.wireOp",EDGE,"E69"),sQuery(id+"F23.wireOp",EDGE,"E70"),sQuery(id+"F23.wireOp",EDGE,"E71"),sQuery(id+"F23.wireOp",EDGE,"E72"),sQuery(id+"F23.wireOp",EDGE,"E73"),sQuery(id+"F23.wireOp",EDGE,"E74"),sQuery(id+"F23.wireOp",EDGE,"E75"),sQuery(id+"F23.wireOp",EDGE,"E76"),sQuery(id+"F23.wireOp",EDGE,"E77"),sQuery(id+"F23.wireOp",EDGE,"E78"),sQuery(id+"F23.wireOp",EDGE,"E79"),sQuery(id+"F23.wireOp",EDGE,"E80"),sQuery(id+"F23.wireOp",EDGE,"E81"),sQuery(id+"F23.wireOp",EDGE,"E82"),sQuery(id+"F23.wireOp",EDGE,"E83"),sQuery(id+"F23.wireOp",EDGE,"E84"),sQuery(id+"F23.wireOp",EDGE,"E85"),sQuery(id+"F23.wireOp",EDGE,"E86"),sQuery(id+"F23.wireOp",EDGE,"E87"),sQuery(id+"F23.wireOp",EDGE,"E88"),sQuery(id+"F23.wireOp",EDGE,"E89"),sQuery(id+"F23.wireOp",EDGE,"E90"),sQuery(id+"F23.wireOp",EDGE,"E92"),sQuery(id+"F23.wireOp",EDGE,"E93"),sQuery(id+"F23.wireOp",EDGE,"E94"),sQuery(id+"F23.wireOp",EDGE,"E95"),sQuery(id+"F23.wireOp",EDGE,"E96"),sQuery(id+"F23.wireOp",EDGE,"E97"),sQuery(id+"F23.wireOp",EDGE,"E98"),sQuery(id+"F23.wireOp",EDGE,"E99"),sQuery(id+"F23.wireOp",EDGE,"E100"),sQuery(id+"F23.wireOp",EDGE,"E141"),sQuery(id+"F23.wireOp",EDGE,"E142"),sQuery(id+"F23.wireOp",EDGE,"E143")])],"isStart":true}),makeQuery(id+"F25.opExtrude","CAP_FACE",FACE,{"disambiguationData":[OSD([sQuery(id+"F23.wireOp",EDGE,"E101"),sQuery(id+"F23.wireOp",EDGE,"E102"),sQuery(id+"F23.wireOp",EDGE,"E103"),sQuery(id+"F23.wireOp",EDGE,"E104"),sQuery(id+"F23.wireOp",EDGE,"E105"),sQuery(id+"F23.wireOp",EDGE,"E106"),sQuery(id+"F23.wireOp",EDGE,"E107"),sQuery(id+"F23.wireOp",EDGE,"E108"),sQuery(id+"F23.wireOp",EDGE,"E109"),sQuery(id+"F23.wireOp",EDGE,"E110"),sQuery(id+"F23.wireOp",EDGE,"E111"),sQuery(id+"F23.wireOp",EDGE,"E112"),sQuery(id+"F23.wireOp",EDGE,"E113"),sQuery(id+"F23.wireOp",EDGE,"E114"),sQuery(id+"F23.wireOp",EDGE,"E115"),sQuery(id+"F23.wireOp",EDGE,"E116"),sQuery(id+"F23.wireOp",EDGE,"E117"),sQuery(id+"F23.wireOp",EDGE,"E118"),sQuery(id+"F23.wireOp",EDGE,"E119"),sQuery(id+"F23.wireOp",EDGE,"E120"),sQuery(id+"F23.wireOp",EDGE,"E121"),sQuery(id+"F23.wireOp",EDGE,"E122"),sQuery(id+"F23.wireOp",EDGE,"E123"),sQuery(id+"F23.wireOp",EDGE,"E124"),sQuery(id+"F23.wireOp",EDGE,"E125"),sQuery(id+"F23.wireOp",EDGE,"E126"),sQuery(id+"F23.wireOp",EDGE,"E127"),sQuery(id+"F23.wireOp",EDGE,"E128"),sQuery(id+"F23.wireOp",EDGE,"E129"),sQuery(id+"F23.wireOp",EDGE,"E130"),sQuery(id+"F23.wireOp",EDGE,"E131"),sQuery(id+"F23.wireOp",EDGE,"E132"),sQuery(id+"F23.wireOp",EDGE,"E133"),sQuery(id+"F23.wireOp",EDGE,"E134"),sQuery(id+"F23.wireOp",EDGE,"E135"),sQuery(id+"F23.wireOp",EDGE,"E136"),sQuery(id+"F23.wireOp",EDGE,"E137"),sQuery(id+"F23.wireOp",EDGE,"E138"),sQuery(id+"F23.wireOp",EDGE,"E139"),sQuery(id+"F23.wireOp",EDGE,"E140")])],"isStart":true})]});}
            var sketch = newSketch(context, id + "F26", { "sketchPlane" : qUnion([Q0])});
            skText(sketch, "E144", { "text": "Pouteau  #36\n", "fontName": "OpenSans-Regular.ttf"});
            const initialGuessF26  = {"E144": [0.02918, 0.01095, -1, 0, 0.00688]};
            skSetInitialGuess(sketch, initialGuessF26);
            skSolve(sketch);
        }
        {
            var Q0;
            Q0 = qSketchRegion(id + "F26", true);
            extrude(context, id + "F27", {"entities" : qUnion([Q0]), "operationType" : NewBodyOperationType.ADD, "depth" : 2.54 * mm, "offsetDistance" : 25.4 * mm});
        }
        {
            var Q0;
            Q0=makeQuery(id+"F13.boolean.opBoolean","COPY",EDGE,{"derivedFrom":makeQuery(id+"F13.opExtrude","SWEPT_EDGE",EDGE,{"disambiguationData":[OSD([sQuery(id+"F0.wireOp",EDGE,"E0.bottom"),sQuery(id+"F0.wireOp",EDGE,"E0.top"),sQuery(id+"F0.wireOp",EDGE,"E0.left"),sQuery(id+"F0.wireOp",EDGE,"E0.right"),sQuery(id+"F12.wireOp",EDGE,"E4.top"),sQuery(id+"F12.wireOp",EDGE,"E4.left")])]})});
            var Q1;
            Q1=makeQuery(id+"F13.boolean.opBoolean","COPY",EDGE,{"derivedFrom":makeQuery(id+"F13.opExtrude","SWEPT_EDGE",EDGE,{"disambiguationData":[OSD([sQuery(id+"F12.wireOp",EDGE,"E4.bottom"),sQuery(id+"F12.wireOp",EDGE,"E4.left")])]})});
            var Q2;
            Q2=makeQuery(id+"F13.boolean.opBoolean","COPY",EDGE,{"derivedFrom":makeQuery(id+"F13.opExtrude","SWEPT_EDGE",EDGE,{"disambiguationData":[OSD([sQuery(id+"F12.wireOp",EDGE,"E4.top"),sQuery(id+"F12.wireOp",EDGE,"E4.right")])]})});
            var Q3;
            Q3=makeQuery(id+"F13.boolean.opBoolean","COPY",EDGE,{"derivedFrom":makeQuery(id+"F13.opExtrude","SWEPT_EDGE",EDGE,{"disambiguationData":[OSD([sQuery(id+"F0.wireOp",EDGE,"E0.bottom"),sQuery(id+"F0.wireOp",EDGE,"E0.top"),sQuery(id+"F0.wireOp",EDGE,"E0.left"),sQuery(id+"F0.wireOp",EDGE,"E0.right"),sQuery(id+"F12.wireOp",EDGE,"E4.bottom"),sQuery(id+"F12.wireOp",EDGE,"E4.right")])]})});
            fillet(context, id + "F28", {"entities" : qUnion([Q0, Q1, Q2, Q3]), "radius" : 6.75 * mm, "tangentPropagation" : true, "allowEdgeOverflow" : false});
        }
    });
